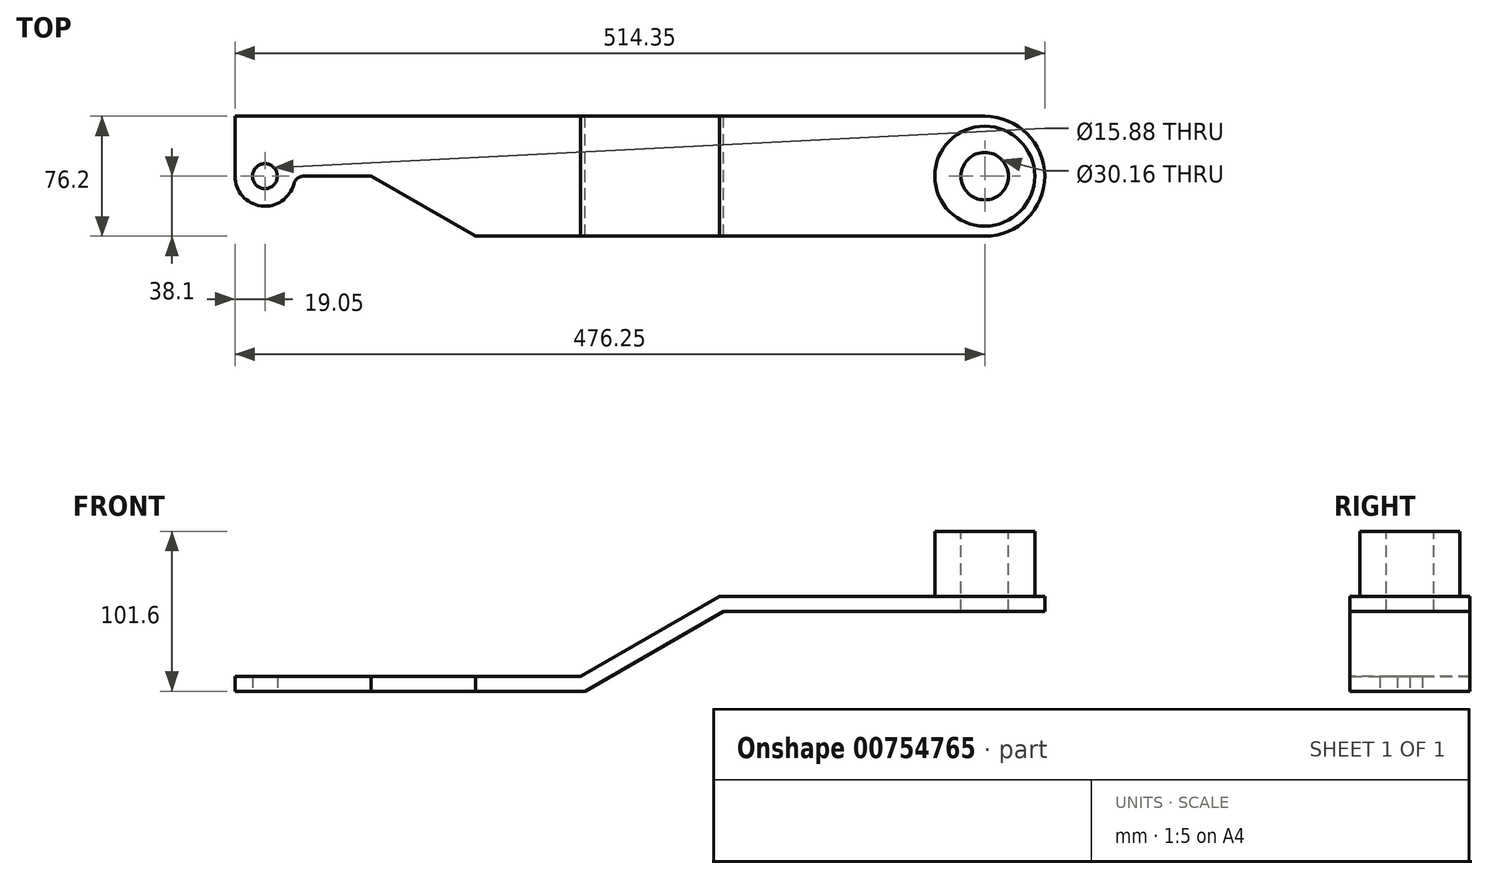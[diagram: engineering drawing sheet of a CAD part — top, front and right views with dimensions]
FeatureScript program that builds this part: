
annotation { "Feature Type Name" : "Feature", "Feature Type Description" : "" }
export const myFeature = defineFeature(function(context is Context, id is Id, definition is map)
    precondition{}
    {
        {
            var Q0;
            Q0=qCreatedBy(makeId("Top.planeOp"),FACE);
            var sketch = newSketch(context, id + "F0", { "sketchPlane" : qUnion([Q0])});
            skLineSegment(sketch, "E0.bottom", {"start": v(0, -38.1) * mm, "end": v(-323.33, -38.1) * mm});
            skLineSegment(sketch, "E0.top", {"start": v(0, 38.1) * mm, "end": v(-476.25, 38.1) * mm});
            skLineSegment(sketch, "E1", {"start": v(0, 0) * mm, "end": v(-323.29, 0) * mm, "construction": true});
            skCircle(sketch, "E2", {"center": v(0, 0) * mm, "radius": 304.8 * mm, "construction": true});
            skLineSegment(sketch, "E3", {"start": v(0, 0) * mm, "end": v(-323.29, -323.29) * mm, "construction": true});
            skLineSegment(sketch, "E4", {"start": v(0, 0) * mm, "end": v(-323.29, 323.29) * mm, "construction": true});
            skLineSegment(sketch, "E5", {"start": v(-215.53, 215.53) * mm, "end": v(-215.53, -215.53) * mm, "construction": true});
            skCircle(sketch, "E6.0", {"center": v(0, 0) * mm, "radius": 457.2 * mm, "construction": true});
            skLineSegment(sketch, "E7", {"start": v(-323.29, 323.29) * mm, "end": v(-323.29, -323.29) * mm, "construction": true});
            skLineSegment(sketch, "E8", {"start": v(-389.73, 0) * mm, "end": v(-432.6, 0) * mm});
            skCircle(sketch, "E9", {"center": v(-457.2, 0) * mm, "radius": 7.94 * mm});
            skArc(sketch, "E10", {"start": v(0, -38.1) * mm, "mid": v(38.1, 0) * mm, "end": v(0, 38.1) * mm});
            skLineSegment(sketch, "E11", {"start": v(-476.25, 0) * mm, "end": v(-476.25, 38.1) * mm});
            skArc(sketch, "E12.trimOffspring", {"start": v(-476.25, 0) * mm, "mid": v(-459.6, -18.9) * mm, "end": v(-438.75, -4.76) * mm});
            skLineSegment(sketch, "E13", {"start": v(-323.29, -38.1) * mm, "end": v(-389.73, 0) * mm});
            skLineSegment(sketch, "E14.trimOffspring", {"start": v(-323.33, -38.08) * mm, "end": v(-323.33, -38.1) * mm});
            skPoint(sketch, "E15.visualSharp", {"position": v(-438.15, 0) * mm});
            skArc(sketch, "E15.filletArc", {"start": v(-432.6, 0) * mm, "mid": v(-436.5, -1.33) * mm, "end": v(-438.75, -4.76) * mm});
            skSolve(sketch);
        }
        {
            var Q0;
            Q0=qSketchRegion(id+"F0",true);
            extrude(context, id + "F1", {"entities" : qUnion([Q0]), "depth" : 9.52 * mm, "offsetDistance" : 25.4 * mm, "hasSecondDirection" : true, "secondDirectionOppositeDirection" : true, "secondDirectionDepth" : 50.8 * mm});
        }
        {
            var Q0;
            Q0=makeQuery(id+"F1.opExtrude","CAP_FACE",FACE,{"disambiguationData":[OSD([sQuery(id+"F0.wireOp",EDGE,"E0.bottom"),sQuery(id+"F0.wireOp",EDGE,"E0.top"),sQuery(id+"F0.wireOp",EDGE,"MrevZkao-XOSf-0SEr-ewuk-3oNjqeuVg15d"),sQuery(id+"F0.wireOp",EDGE,"OW4nvHeo-bfOe-Kfip-d3tS-PoIOrMrv3fz6"),sQuery(id+"F0.wireOp",EDGE,"j4LAOJZS-ABN7-WX8l-AeGy-pPzTyCXKroeO"),sQuery(id+"F0.wireOp",EDGE,"E8"),sQuery(id+"F0.wireOp",EDGE,"f590f8ba-0d23-4390-9766-3ab41873eea9.filletArc"),sQuery(id+"F0.wireOp",EDGE,"SYAwkZWX-SYEm-uCO0-AMka-laG2Mx1onckF"),sQuery(id+"F0.wireOp",EDGE,"E9"),sQuery(id+"F0.wireOp",EDGE,"E10")])],"isStart":false});
            var sketch = newSketch(context, id + "F2", { "sketchPlane" : qUnion([Q0])});
            skCircle(sketch, "E16", {"center": v(0, 0) * mm, "radius": 31.75 * mm});
            skSolve(sketch);
        }
        {
            var Q0;
            Q0=qSketchRegion(id+"F2",true);
            extrude(context, id + "F3", {"entities" : qUnion([Q0]), "operationType" : NewBodyOperationType.ADD, "depth" : 41.27 * mm, "offsetDistance" : 25.4 * mm});
        }
        {
            var Q0;
            Q0=makeQuery(id+"F3.opExtrude","CAP_FACE",FACE,{"disambiguationData":[OSD([sQuery(id+"F2.wireOp",EDGE,"E16")])],"isStart":false});
            var sketch = newSketch(context, id + "F4", { "sketchPlane" : qUnion([Q0])});
            skCircle(sketch, "E17", {"center": v(0, 0) * mm, "radius": 15.08 * mm});
            skSolve(sketch);
        }
        {
            var Q0;
            Q0=qSketchRegion(id+"F4",true);
            extrude(context, id + "F5", {"entities" : qUnion([Q0]), "operationType" : NewBodyOperationType.REMOVE, "endBound" : BoundingType.THROUGH_ALL, "oppositeDirection" : true, "depth" : 25.4 * mm, "offsetDistance" : 25.4 * mm});
        }
        {
            var Q0;
            Q0=makeQuery(id+"F1.opExtrude","SWEPT_FACE",FACE,{"disambiguationData":[OSD([sQuery(id+"F0.wireOp",EDGE,"E0.top"),sQuery(id+"F0.wireOp",EDGE,"j4LAOJZS-ABN7-WX8l-AeGy-pPzTyCXKroeO")])]});
            var sketch = newSketch(context, id + "F6", { "sketchPlane" : qUnion([Q0])});
            skLineSegment(sketch, "E18.bottom", {"start": v(254, -50.8) * mm, "end": v(-101.6, -50.8) * mm});
            skLineSegment(sketch, "E18.top", {"start": v(166.01, 0) * mm, "end": v(-101.6, 0) * mm});
            skLineSegment(sketch, "E18.right", {"start": v(-101.6, -50.8) * mm, "end": v(-101.6, 0) * mm});
            skLineSegment(sketch, "E19", {"start": v(254, -50.8) * mm, "end": v(166.01, 0) * mm});
            skLineSegment(sketch, "E20.bottom", {"start": v(168.56, 9.52) * mm, "end": v(524.16, 9.52) * mm});
            skLineSegment(sketch, "E20.top", {"start": v(256.55, -41.28) * mm, "end": v(524.16, -41.28) * mm});
            skLineSegment(sketch, "E20.right", {"start": v(524.16, 9.52) * mm, "end": v(524.16, -41.28) * mm});
            skLineSegment(sketch, "E21", {"start": v(168.56, 9.53) * mm, "end": v(256.55, -41.28) * mm});
            skSolve(sketch);
        }
        {
            var Q0;
            Q0=qSketchRegion(id+"F6",true);
            extrude(context, id + "F7", {"entities" : qUnion([Q0]), "operationType" : NewBodyOperationType.REMOVE, "endBound" : BoundingType.THROUGH_ALL, "oppositeDirection" : true, "depth" : 25.4 * mm, "offsetDistance" : 25.4 * mm});
        }
    });
